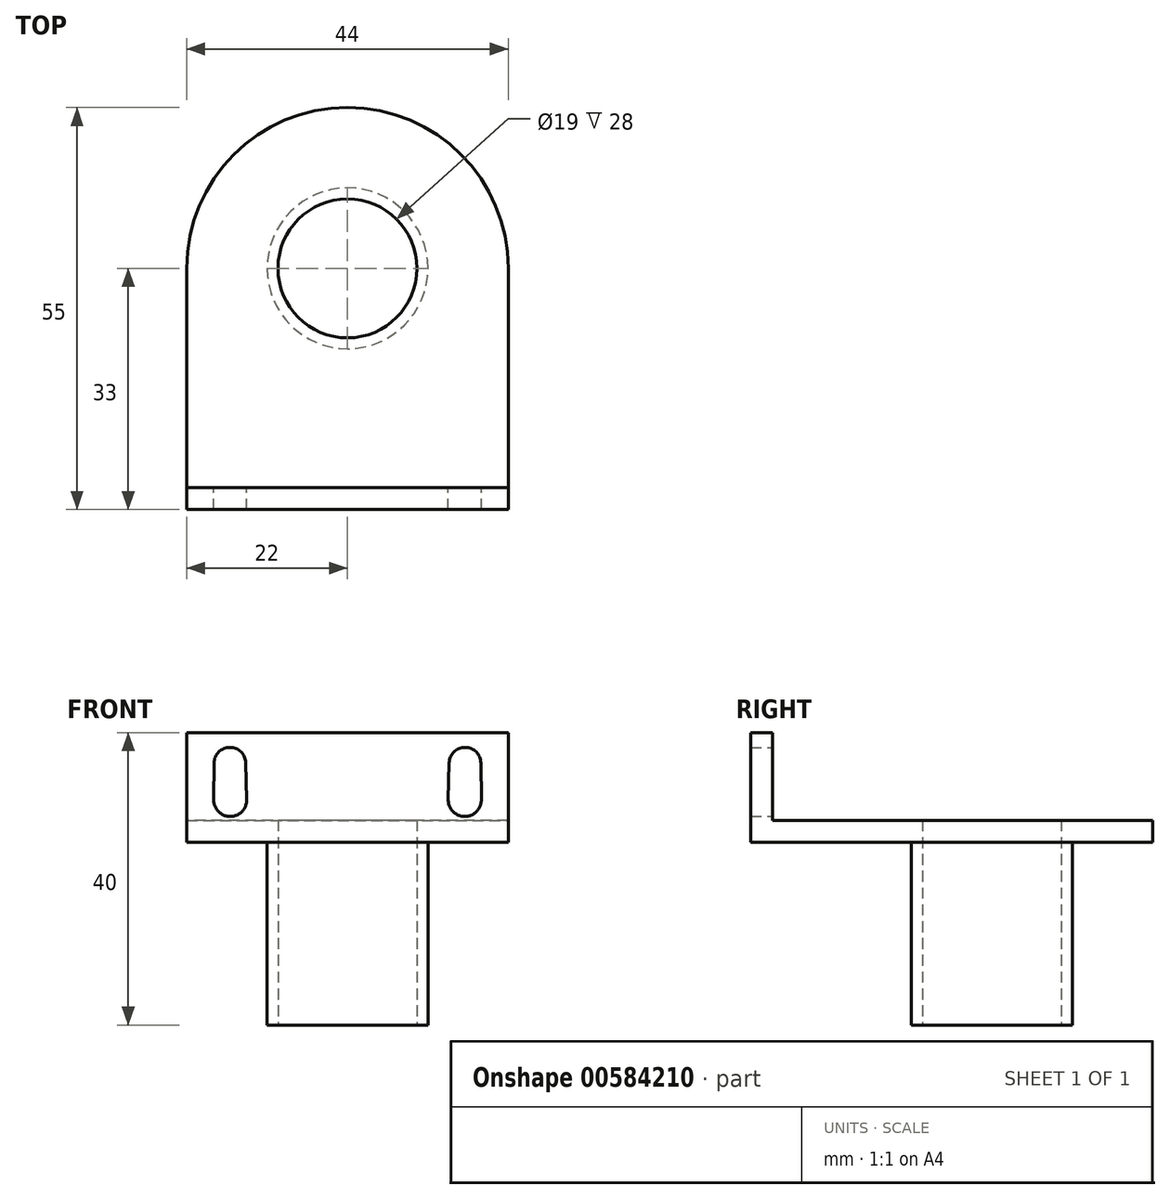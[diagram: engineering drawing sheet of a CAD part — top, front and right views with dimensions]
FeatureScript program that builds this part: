
annotation { "Feature Type Name" : "Feature", "Feature Type Description" : "" }
export const myFeature = defineFeature(function(context is Context, id is Id, definition is map)
    precondition{}
    {
        {
            var Q0;
            Q0=qCreatedBy(makeId("Top.planeOp"),FACE);
            var sketch = newSketch(context, id + "F0", { "sketchPlane" : qUnion([Q0])});
            skCircle(sketch, "E0", {"center": v(0, 0) * mm, "radius": 9.5 * mm});
            skCircle(sketch, "E1", {"center": v(0, 0) * mm, "radius": 11 * mm});
            skCircle(sketch, "E2", {"center": v(0, 0) * mm, "radius": 22 * mm});
            skLineSegment(sketch, "E3", {"start": v(-22, 0) * mm, "end": v(-22, -30) * mm});
            skLineSegment(sketch, "E4", {"start": v(-22, -30) * mm, "end": v(22, -30) * mm});
            skLineSegment(sketch, "E5", {"start": v(22, -30) * mm, "end": v(22, 0) * mm});
            skLineSegment(sketch, "E6", {"start": v(-22, -30) * mm, "end": v(-22, -33) * mm});
            skLineSegment(sketch, "E7", {"start": v(-22, -33) * mm, "end": v(22, -33) * mm});
            skLineSegment(sketch, "E8", {"start": v(22, -33) * mm, "end": v(22, -30) * mm});
            skSolve(sketch);
        }
        {
            var Q0;
            {var subQ0=sQuery(id+"F0.wireOp",EDGE,"E3");Q0=makeQuery(id+"F0.imprint","IMPRINT",FACE,{"disambiguationData":[TD([[makeQuery(id+"F0.imprint","IMPRINT",EDGE,{"derivedFrom":subQ0}),1.0]])]});}
            var Q1;
            Q1=makeQuery(id+"F0.imprint","IMPRINT",FACE,{"disambiguationData":[TD([[makeQuery(id+"F0.imprint","IMPRINT",EDGE,{"derivedFrom":sQuery(id+"F0.wireOp",EDGE,"E1")}),-1.0]])]});
            var Q2;
            Q2=makeQuery(id+"F0.imprint","IMPRINT",FACE,{"disambiguationData":[TD([[makeQuery(id+"F0.imprint","IMPRINT",EDGE,{"derivedFrom":sQuery(id+"F0.wireOp",EDGE,"E0")}),-1.0]])]});
            extrude(context, id + "F1", {"entities" : qUnion([Q0, Q1, Q2]), "depth" : 3 * mm, "offsetDistance" : 25 * mm});
        }
        {
            var Q0;
            Q0=makeQuery(id+"F0.imprint","IMPRINT",FACE,{"disambiguationData":[TD([[makeQuery(id+"F0.imprint","IMPRINT",EDGE,{"derivedFrom":sQuery(id+"F0.wireOp",EDGE,"E4")}),-1.0]])]});
            extrude(context, id + "F2", {"entities" : qUnion([Q0]), "operationType" : NewBodyOperationType.ADD, "depth" : 15 * mm, "offsetDistance" : 25 * mm});
        }
        {
            var Q0;
            Q0=makeQuery(id+"F0.imprint","IMPRINT",FACE,{"disambiguationData":[TD([[makeQuery(id+"F0.imprint","IMPRINT",EDGE,{"derivedFrom":sQuery(id+"F0.wireOp",EDGE,"E0")}),-1.0]])]});
            extrude(context, id + "F3", {"entities" : qUnion([Q0]), "operationType" : NewBodyOperationType.ADD, "depth" : -25 * mm, "offsetDistance" : 25 * mm});
        }
        {
            var Q0;
            Q0=qCreatedBy(makeId("Front.planeOp"),FACE);
            var sketch = newSketch(context, id + "F4", { "sketchPlane" : qUnion([Q0])});
            skCircle(sketch, "E9", {"center": v(-16.08, 10.81) * mm, "radius": 2.16 * mm});
            skCircle(sketch, "E10", {"center": v(-16.05, 5.78) * mm, "radius": 2.26 * mm});
            skLineSegment(sketch, "E11", {"start": v(-18.25, 10.84) * mm, "end": v(-18.3, 5.8) * mm});
            skLineSegment(sketch, "E12", {"start": v(-13.92, 10.87) * mm, "end": v(-13.79, 5.84) * mm});
            skLineSegment(sketch, "E13.MirrorCS", {"start": v(13.92, 10.87) * mm, "end": v(13.79, 5.84) * mm});
            skLineSegment(sketch, "E14.MirrorCS", {"start": v(18.25, 10.84) * mm, "end": v(18.3, 5.8) * mm});
            skCircle(sketch, "E15.MirrorC", {"center": v(16.08, 10.81) * mm, "radius": 2.16 * mm});
            skCircle(sketch, "E16.MirrorC", {"center": v(16.05, 5.78) * mm, "radius": 2.26 * mm});
            skSolve(sketch);
        }
        {
            var Q0;
            Q0 = qSketchRegion(id + "F4", true);
            extrude(context, id + "F5", {"entities" : qUnion([Q0]), "operationType" : NewBodyOperationType.REMOVE, "oppositeDirection" : true, "depth" : -50 * mm, "offsetDistance" : 25 * mm});
        }
    });
